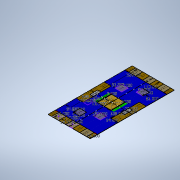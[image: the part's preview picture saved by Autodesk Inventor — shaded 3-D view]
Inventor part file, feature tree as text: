
AUTODESK INVENTOR PART (.ipt)
format: ipt  version: 2020 (Build 240168000, 168)  size: 252,928 bytes
history: native  units: in
note: dims shown in document units (in); Inventor stores cm internally (conversion verified against a paired STEP export)
features: sketch x1, other x1
ambient origin geometry x8: Origin, YZ Plane, XZ Plane, XY Plane, X Axis, Y Axis, Z Axis, Center Point
feature tree (2):
  sketch  "Sketch1"  dims[d0=324.0in d1=648.0in d25=56.0in d26=34.0in d27=40.0in d34=52.0in d35=52.0in d60=52.0in d61=52.0in d71=52.0in d72=52.0in d77=108.0in d78=110.0in d82=54.0in d83=108.0in d85=110.0in d87=81.0in d93=110.0in d95=81.0in d97=52.0in d99=52.0in d102=54.0in d103=54.0in d105=54.0in d111=3.0in d112=3.0in d113=27.0in d114=30.0in]
  other  "Image2"
